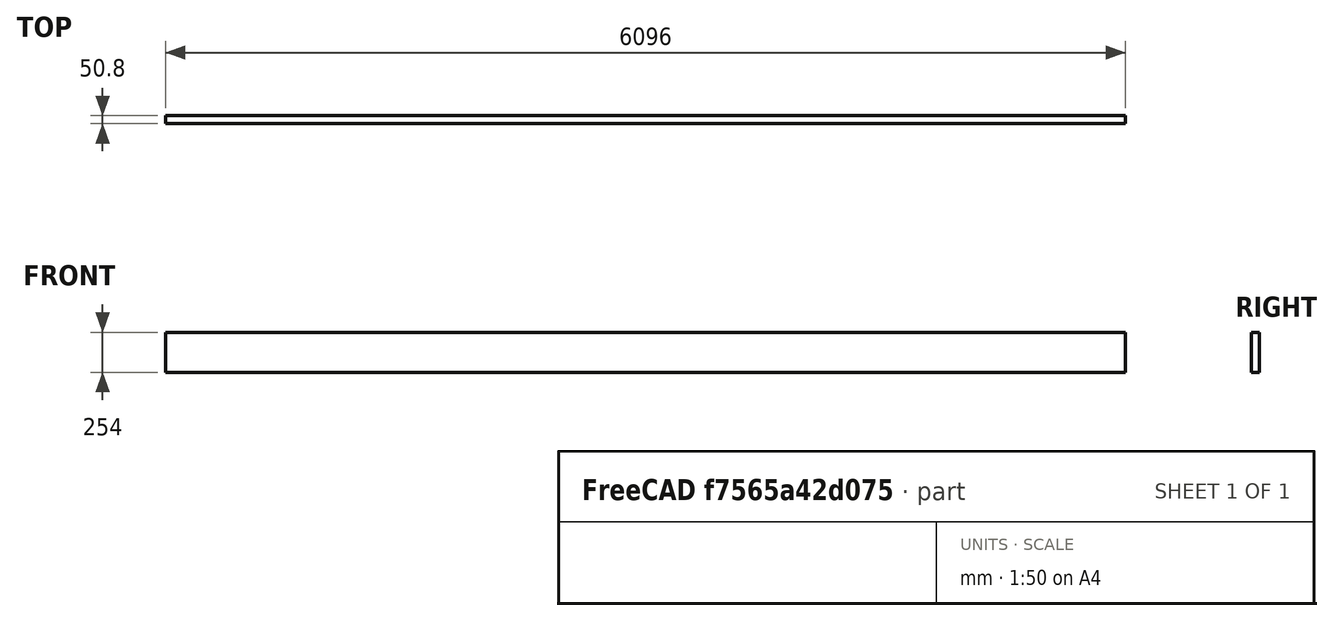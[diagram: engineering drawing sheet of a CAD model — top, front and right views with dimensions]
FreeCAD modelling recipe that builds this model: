
FCSTD DOCUMENT  (FreeCAD 0.20R29177 (Git))
Label: CrossMemberFront
License: All rights reserved
LicenseURL: http://en.wikipedia.org/wiki/All_rights_reserved
objects: Sketcher::SketchObject×1, PartDesign::Pad×1, PartDesign::Body×1
note: 4 computed .brp shape members not serialized (recipe doc carries the construction recipe); baked Part::Feature solids carry a one-line shape summary decoded from their .brp

FEATURE [Sketcher::SketchObject] Sketch
  FullyConstrained = true
  MapMode = 5
  Placement = pos=(0,0,0) rot=(0.57735,0.57735,0.57735;2.0944rad)
  Support = -> [YZ_Plane]
  sketch-geometry (4):
    g0: LineSegment StartX=0 StartY=0 StartZ=0 EndX=50.8 EndY=0 EndZ=0
    g1: LineSegment StartX=50.8 StartY=0 StartZ=0 EndX=50.8 EndY=254 EndZ=0
    g2: LineSegment StartX=50.8 StartY=254 StartZ=0 EndX=0 EndY=254 EndZ=0
    g3: LineSegment StartX=0 StartY=254 StartZ=0 EndX=0 EndY=0 EndZ=0
  constraints (11):
    c: Coincident(g0,g1)
    c: Coincident(g1,g2)
    c: Coincident(g2,g3)
    c: Coincident(g3,g0)
    c: Horizontal(g0)
    c: Horizontal(g2)
    c: Vertical(g1)
    c: Vertical(g3)
    c: Coincident(g0,g-1)
    c: DistanceX(g2,g2) = 50.8
    c: DistanceY(g3,g3) = 254
FEATURE [PartDesign::Pad] Pad
  Direction = (1,-2e-16,3e-16)
  Length = 6096
  Length2 = 9.525
  Placement = pos=(0,0,0) rot=(0.57735,0.57735,0.57735;2.0944rad)
  Profile = -> Sketch
  ReferenceAxis = -> Sketch [N_Axis]
  Type = 0
FEATURE [PartDesign::Body] Body
  Group = -> [Sketch,Pad]
  Origin = -> Origin
  Tip = -> Pad
